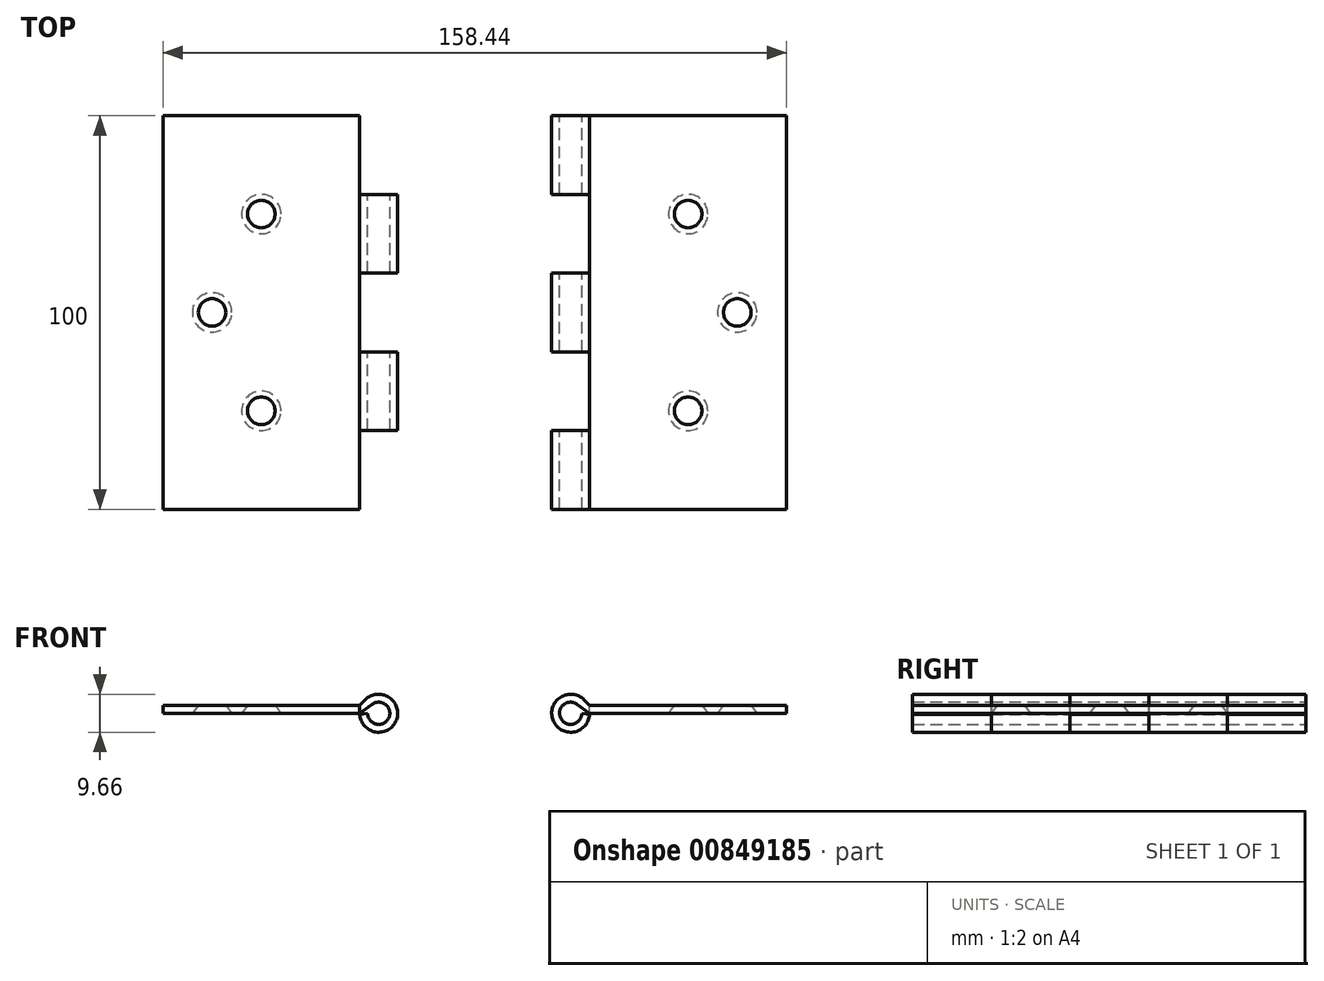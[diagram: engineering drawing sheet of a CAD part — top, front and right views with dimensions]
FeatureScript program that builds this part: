
annotation { "Feature Type Name" : "Feature", "Feature Type Description" : "" }
export const myFeature = defineFeature(function(context is Context, id is Id, definition is map)
    precondition{}
    {
        {
            var Q0;
            Q0=qCreatedBy(makeId("Front.planeOp"),FACE);
            var sketch = newSketch(context, id + "F0", { "sketchPlane" : qUnion([Q0])});
            skLineSegment(sketch, "E0.bottom", {"start": v(-10.38, 25) * mm, "end": v(39.62, 25) * mm});
            skLineSegment(sketch, "E0.top", {"start": v(-10.38, 23) * mm, "end": v(39.62, 23) * mm});
            skLineSegment(sketch, "E0.right", {"start": v(39.62, 25) * mm, "end": v(39.62, 23) * mm});
            skLineSegment(sketch, "E1", {"start": v(-10.38, 25) * mm, "end": v(-11.8, 26.4) * mm});
            skArc(sketch, "E2", {"start": v(-11.8, 26.4) * mm, "mid": v(-19.72, 21.27) * mm, "end": v(-10.4, 22.72) * mm});
            skLineSegment(sketch, "E3", {"start": v(-15.21, 23) * mm, "end": v(-15.21, 25.82) * mm});
            skArc(sketch, "E4", {"start": v(-13.56, 25.28) * mm, "mid": v(-17.73, 21.7) * mm, "end": v(-12.38, 23) * mm});
            skLineSegment(sketch, "E5", {"start": v(-10.38, 23) * mm, "end": v(-13.56, 25.28) * mm});
            skLineSegment(sketch, "E6", {"start": v(-12.38, 23) * mm, "end": v(-10.4, 22.72) * mm});
            skSolve(sketch);
        }
        {
            var Q0;
            Q0=makeQuery(id+"F0.imprint","IMPRINT",FACE,{"disambiguationData":[TD([[makeQuery(id+"F0.imprint","IMPRINT",EDGE,{"derivedFrom":sQuery(id+"F0.wireOp",EDGE,"E0.bottom")}),-1.0]])]});
            extrude(context, id + "F1", {"entities" : qUnion([Q0]), "depth" : 100 * mm, "offsetDistance" : 25 * mm});
        }
        {
            var Q0;
            Q0=makeQuery(id+"F1.opExtrude","SWEPT_FACE",FACE,{"disambiguationData":[OSD([sQuery(id+"F0.wireOp",EDGE,"E0.top")])]});
            var sketch = newSketch(context, id + "F2", { "sketchPlane" : qUnion([Q0])});
            skCircle(sketch, "E7", {"center": v(27.12, 50) * mm, "radius": 5 * mm});
            skPoint(sketch, "E8.orphan", {"position": v(14.62, 100) * mm});
            skPoint(sketch, "E9.end.orphan", {"position": v(14.62, 0) * mm});
            skCircle(sketch, "E10", {"center": v(14.62, 75) * mm, "radius": 5 * mm});
            skCircle(sketch, "E11", {"center": v(14.62, 25) * mm, "radius": 5 * mm});
            skSolve(sketch);
        }
        {
            var Q0;
            Q0=makeQuery(id+"F1.opExtrude","SWEPT_FACE",FACE,{"disambiguationData":[OSD([sQuery(id+"F0.wireOp",EDGE,"E0.bottom")])]});
            var sketch = newSketch(context, id + "F3", { "sketchPlane" : qUnion([Q0])});
            skCircle(sketch, "E12", {"center": v(14.62, -25) * mm, "radius": 3.5 * mm});
            skCircle(sketch, "E13", {"center": v(27.12, -50) * mm, "radius": 3.5 * mm});
            skCircle(sketch, "E14", {"center": v(14.62, -75) * mm, "radius": 3.5 * mm});
            skSolve(sketch);
        }
        {
            var Q1;
            Q1=makeQuery(id+"F2.imprint","IMPRINT",FACE,{"disambiguationData":[TD([[makeQuery(id+"F2.imprint","IMPRINT",EDGE,{"derivedFrom":sQuery(id+"F2.wireOp",EDGE,"E10")}),1.0]])]});
            var Q2;
            Q2=makeQuery(id+"F3.imprint","IMPRINT",FACE,{"disambiguationData":[TD([[makeQuery(id+"F3.imprint","IMPRINT",EDGE,{"derivedFrom":sQuery(id+"F3.wireOp",EDGE,"E14")}),1.0]])]});
            loft(context, id + "F4", {"operationType" : NewBodyOperationType.REMOVE, "sheetProfilesArray" : [{ "sheetProfileEntities" : qUnion([Q1]) }, { "sheetProfileEntities" : qUnion([Q2]) }]});
        }
        {
            var Q1;
            Q1=makeQuery(id+"F2.imprint","IMPRINT",FACE,{"disambiguationData":[TD([[makeQuery(id+"F2.imprint","IMPRINT",EDGE,{"derivedFrom":sQuery(id+"F2.wireOp",EDGE,"E7")}),1.0]])]});
            var Q2;
            Q2=makeQuery(id+"F3.imprint","IMPRINT",FACE,{"disambiguationData":[TD([[makeQuery(id+"F3.imprint","IMPRINT",EDGE,{"derivedFrom":sQuery(id+"F3.wireOp",EDGE,"E13")}),1.0]])]});
            loft(context, id + "F5", {"operationType" : NewBodyOperationType.REMOVE, "sheetProfilesArray" : [{ "sheetProfileEntities" : qUnion([Q1]) }, { "sheetProfileEntities" : qUnion([Q2]) }]});
        }
        {
            var Q1;
            Q1=makeQuery(id+"F2.imprint","IMPRINT",FACE,{"disambiguationData":[TD([[makeQuery(id+"F2.imprint","IMPRINT",EDGE,{"derivedFrom":sQuery(id+"F2.wireOp",EDGE,"E11")}),1.0]])]});
            var Q2;
            Q2=makeQuery(id+"F3.imprint","IMPRINT",FACE,{"disambiguationData":[TD([[makeQuery(id+"F3.imprint","IMPRINT",EDGE,{"derivedFrom":sQuery(id+"F3.wireOp",EDGE,"E12")}),1.0]])]});
            loft(context, id + "F6", {"operationType" : NewBodyOperationType.REMOVE, "sheetProfilesArray" : [{ "sheetProfileEntities" : qUnion([Q1]) }, { "sheetProfileEntities" : qUnion([Q2]) }]});
        }
        {
            var Q0;
            Q0=qCreatedBy(makeId("Right.planeOp"),FACE);
            cPlane(context, id + "F7", {"entities" : qUnion([Q0]), "cplaneType" : CPlaneType.OFFSET, "offset" : 39.6 * mm, "oppositeDirection" : true, "width" : 150 * mm, "height" : 150 * mm});
        }
        {
            var Q0;
            Q0=makeQuery(id+"F1.opExtrude","SWEPT_BODY",BODY,{"disambiguationData":[OSD([sQuery(id+"F0.wireOp",EDGE,"E0.bottom"),sQuery(id+"F0.wireOp",EDGE,"E0.top"),sQuery(id+"F0.wireOp",EDGE,"E0.right"),sQuery(id+"F0.wireOp",EDGE,"E1"),sQuery(id+"F0.wireOp",EDGE,"E2"),sQuery(id+"F0.wireOp",EDGE,"E4"),sQuery(id+"F0.wireOp",EDGE,"E5"),sQuery(id+"F0.wireOp",EDGE,"E6")])]});
            var Q1;
            Q1=qCreatedBy(id+"F7.planeOp",FACE);
            mirror(context, id + "F8", {"entities" : qUnion([Q0]), "mirrorPlane" : qUnion([Q1])});
        }
        {
            var Q0;
            Q0=makeQuery(id+"F2.imprint","IMPRINT",FACE,{"disambiguationData":[TD([[makeQuery(id+"F2.imprint","IMPRINT",EDGE,{"derivedFrom":sQuery(id+"F2.wireOp",EDGE,"E7")}),-1.0]])]});
            cPlane(context, id + "F9", {"entities" : qUnion([Q0]), "cplaneType" : CPlaneType.OFFSET, "offset" : 0.6 * mm, "width" : 150 * mm, "height" : 150 * mm});
        }
        {
            var Q0;
            Q0=qCreatedBy(id+"F9.planeOp",FACE);
            var sketch = newSketch(context, id + "F10", { "sketchPlane" : qUnion([Q0])});
            skLineSegment(sketch, "E15.0", {"start": v(-68.82, 100) * mm, "end": v(-68.82, 0) * mm});
            skLineSegment(sketch, "E16.0", {"start": v(-10.38, 100) * mm, "end": v(-10.38, 0) * mm});
            skLineSegment(sketch, "E17.bottom", {"start": v(-68.82, 100) * mm, "end": v(-48.82, 100) * mm});
            skLineSegment(sketch, "E17.top", {"start": v(-68.82, 80) * mm, "end": v(-48.82, 80) * mm});
            skLineSegment(sketch, "E17.left", {"start": v(-68.82, 100) * mm, "end": v(-68.82, 80) * mm});
            skLineSegment(sketch, "E17.right", {"start": v(-48.82, 100) * mm, "end": v(-48.82, 80) * mm});
            skLineSegment(sketch, "E18.bottom", {"start": v(-30.38, 80) * mm, "end": v(-10.38, 80) * mm});
            skLineSegment(sketch, "E18.top", {"start": v(-30.38, 60) * mm, "end": v(-10.38, 60) * mm});
            skLineSegment(sketch, "E18.left", {"start": v(-30.38, 80) * mm, "end": v(-30.38, 60) * mm});
            skLineSegment(sketch, "E18.right", {"start": v(-10.38, 80) * mm, "end": v(-10.38, 60) * mm});
            skLineSegment(sketch, "E19.bottom", {"start": v(-48.82, 60) * mm, "end": v(-68.82, 60) * mm});
            skLineSegment(sketch, "E19.top", {"start": v(-48.82, 40) * mm, "end": v(-68.82, 40) * mm});
            skLineSegment(sketch, "E19.left", {"start": v(-48.82, 60) * mm, "end": v(-48.82, 40) * mm});
            skLineSegment(sketch, "E19.right", {"start": v(-68.82, 60) * mm, "end": v(-68.82, 40) * mm});
            skLineSegment(sketch, "E20.bottom", {"start": v(-30.38, 40) * mm, "end": v(-10.38, 40) * mm});
            skLineSegment(sketch, "E20.top", {"start": v(-30.38, 20) * mm, "end": v(-10.38, 20) * mm});
            skLineSegment(sketch, "E20.left", {"start": v(-30.38, 40) * mm, "end": v(-30.38, 20) * mm});
            skLineSegment(sketch, "E20.right", {"start": v(-10.38, 40) * mm, "end": v(-10.38, 20) * mm});
            skLineSegment(sketch, "E21.bottom", {"start": v(-68.82, 0) * mm, "end": v(-48.82, 0) * mm});
            skLineSegment(sketch, "E21.top", {"start": v(-68.82, 20) * mm, "end": v(-48.82, 20) * mm});
            skLineSegment(sketch, "E21.left", {"start": v(-68.82, 0) * mm, "end": v(-68.82, 20) * mm});
            skLineSegment(sketch, "E21.right", {"start": v(-48.82, 0) * mm, "end": v(-48.82, 20) * mm});
            skSolve(sketch);
        }
        {
            var Q0;
            Q0=makeQuery(id+"F10.imprint","IMPRINT",FACE,{"disambiguationData":[TD([[makeQuery(id+"F10.imprint","IMPRINT",EDGE,{"derivedFrom":sQuery(id+"F10.wireOp",EDGE,"E17.bottom")}),-1.0]])]});
            var Q1;
            Q1=makeQuery(id+"F10.imprint","IMPRINT",FACE,{"disambiguationData":[TD([[makeQuery(id+"F10.imprint","IMPRINT",EDGE,{"derivedFrom":sQuery(id+"F10.wireOp",EDGE,"E19.bottom")}),1.0]])]});
            var Q2;
            Q2=makeQuery(id+"F10.imprint","IMPRINT",FACE,{"disambiguationData":[TD([[makeQuery(id+"F10.imprint","IMPRINT",EDGE,{"derivedFrom":sQuery(id+"F10.wireOp",EDGE,"E21.bottom")}),1.0]])]});
            extrude(context, id + "F11", {"entities" : qUnion([Q0, Q1, Q2]), "operationType" : NewBodyOperationType.REMOVE, "endBound" : BoundingType.SYMMETRIC, "depth" : 25 * mm, "offsetDistance" : 25 * mm});
        }
        {
            var Q0;
            Q0=makeQuery(id+"F10.imprint","IMPRINT",FACE,{"disambiguationData":[TD([[makeQuery(id+"F10.imprint","IMPRINT",EDGE,{"derivedFrom":sQuery(id+"F10.wireOp",EDGE,"E18.bottom")}),-1.0]])]});
            var Q1;
            Q1=makeQuery(id+"F10.imprint","IMPRINT",FACE,{"disambiguationData":[TD([[makeQuery(id+"F10.imprint","IMPRINT",EDGE,{"derivedFrom":sQuery(id+"F10.wireOp",EDGE,"E20.bottom")}),-1.0]])]});
            extrude(context, id + "F12", {"entities" : qUnion([Q0, Q1]), "operationType" : NewBodyOperationType.REMOVE, "endBound" : BoundingType.SYMMETRIC, "depth" : 25 * mm, "offsetDistance" : 25 * mm});
        }
    });
